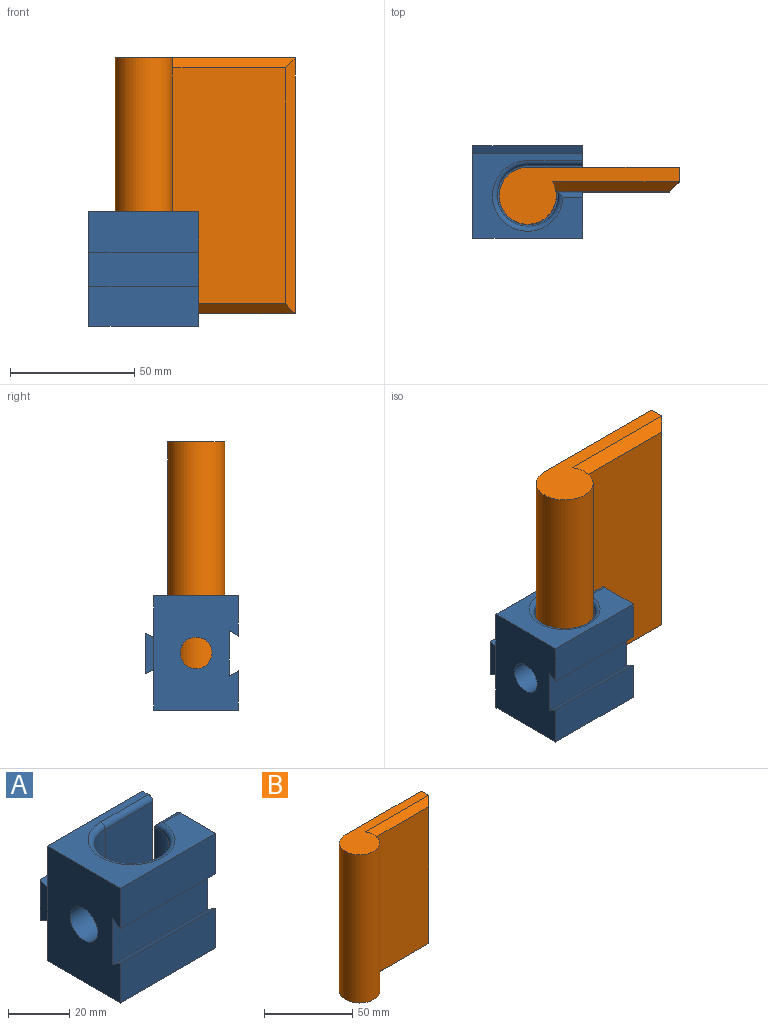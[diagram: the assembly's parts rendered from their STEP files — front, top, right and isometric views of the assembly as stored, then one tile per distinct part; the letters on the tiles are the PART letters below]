
ASSEMBLY  parts=2 mates=1
PART A: 25 faces, bbox 44.2x37.3x46 mm
  f0: plane 44.22x16.73mm, normal (0,1,0), area 739.4mm2, adj f2,f10,f12,f19
  f1: plane 44.22x15.8mm, normal (0,-1,0), area 698.8mm2, adj f2,f5,f10,f17
  f2: plane 46.02x34.02mm, normal (1,0,0), area 1059.3mm2, adj f0,f1,f4,f5,f6,f7,f9,f11
  f3: cylinder r=8.5mm len=17mm, axis (0,0,-1), area 267mm2, adj f4,f5
  f4: plane 34.36x24.5mm, normal (0,0,1), area 383.1mm2, adj f2,f3,f6,f7,f8
  f5: plane 44.22x34mm, normal (0,0,-1), area 1276.4mm2, adj f1,f2,f3,f9,f10
  f6: plane 39x9.94mm, normal (0,1,0), area 387.8mm2, adj f2,f4,f8,f13
  f7: plane 39x22.11mm, normal (0,-1,0), area 862.2mm2, adj f2,f4,f8,f15
  f8: cylinder r=12.25mm len=39mm, axis (0,0,-1), area 2173.7mm2, adj f4,f6,f7,f14,f24
  f9: plane 44.22x16.28mm, normal (0,1,0), area 719.5mm2, adj f2,f5,f10,f20
  f10: plane 46.02x34.02mm, normal (-1,0,0), area 1374.6mm2, adj f0,f1,f5,f9,f11,f12,f16,f17
  f11: plane 44.22x16.2mm, normal (0,-1,0), area 716.2mm2, adj f2,f10,f12,f16
  f12: plane 44.22x34mm, normal (0,0,1), area 705.5mm2, adj f0,f2,f10,f11,f13,f14,f15
  f13: cylinder r=2mm len=9.94mm, axis (1,0,0), area 28mm2, adj f2,f6,f12,f14
  f14: torus R=14.25mm, axis (0,0,1), area 193.7mm2, adj f8,f12,f13,f15
  f15: cylinder r=2mm len=22.11mm, axis (-1,0,0), area 69.5mm2, adj f2,f7,f12,f14
  f16: plane 44.22x3.72mm, normal (0,0.5,-0.87), area 190.1mm2, adj f2,f10,f11,f18
  f17: plane 44.22x3.72mm, normal (0,0.5,0.87), area 190.1mm2, adj f1,f2,f10,f18
  f18: plane 44.22x18.3mm, normal (0,-1,0), area 809.2mm2, adj f2,f10,f16,f17
  f19: plane 44.2x3.3mm, normal (0,-0.46,0.89), area 164.3mm2, adj f0,f21,f22,f23
  f20: plane 44.21x3.31mm, normal (0,-0.46,-0.89), area 164.4mm2, adj f9,f21,f22,f23
  f21: plane 44.2x16.44mm, normal (0,1,0), area 726.5mm2, adj f19,f20,f22,f23
  f22: plane 16.45x3.32mm, normal (1,0,0), area 48.6mm2, adj f2,f19,f20,f21
  f23: plane 16.45x3.31mm, normal (-1,0,0), area 48.5mm2, adj f10,f19,f20,f21
  f24: cylinder r=6.41mm len=12.83mm, axis (-1,0,0), area 397.3mm2, adj f8,f10
PART B: 9 faces, bbox 72.5x23x103 mm
  f0: cylinder r=11.5mm len=103mm, axis (0,0,-1), area 5769mm2, adj f1,f3,f4,f5,f6,f8
  f1: plane 95x45.62mm, normal (0,-1,0), area 4333.8mm2, adj f0,f6,f7,f8
  f2: plane 103x5.85mm, normal (1,0,0), area 602.5mm2, adj f3,f4,f5,f7
  f3: plane 103x61mm, normal (0,1,0), area 6283mm2, adj f0,f2,f4,f5
  f4: plane 72.5x23mm, normal (0,0,1), area 730.7mm2, adj f0,f2,f3,f6
  f5: plane 72.5x23mm, normal (0,0,-1), area 730.7mm2, adj f0,f2,f3,f8
  f6: plane 50.98x4mm, normal (0,-0.71,0.71), area 272.5mm2, adj f0,f1,f4,f7
  f7: plane 103x4mm, normal (0.71,-0.71,0), area 560mm2, adj f1,f2,f6,f8
  f8: plane 50.98x4mm, normal (0,-0.71,-0.71), area 272.5mm2, adj f0,f1,f5,f7
PLACE A rot(axis=(-0.95,-0.09,0.31),0deg) t=(-34.09,-92.87,-87.37)mm
PLACE B rot(axis=(-0.95,-0.09,0.31),0deg) t=(-34.09,-92.87,-82.37)mm
MATE slider A.f3 <-> B.f0  axis (0,0,1) through (-34.09,-92.87,-82.37)mm
